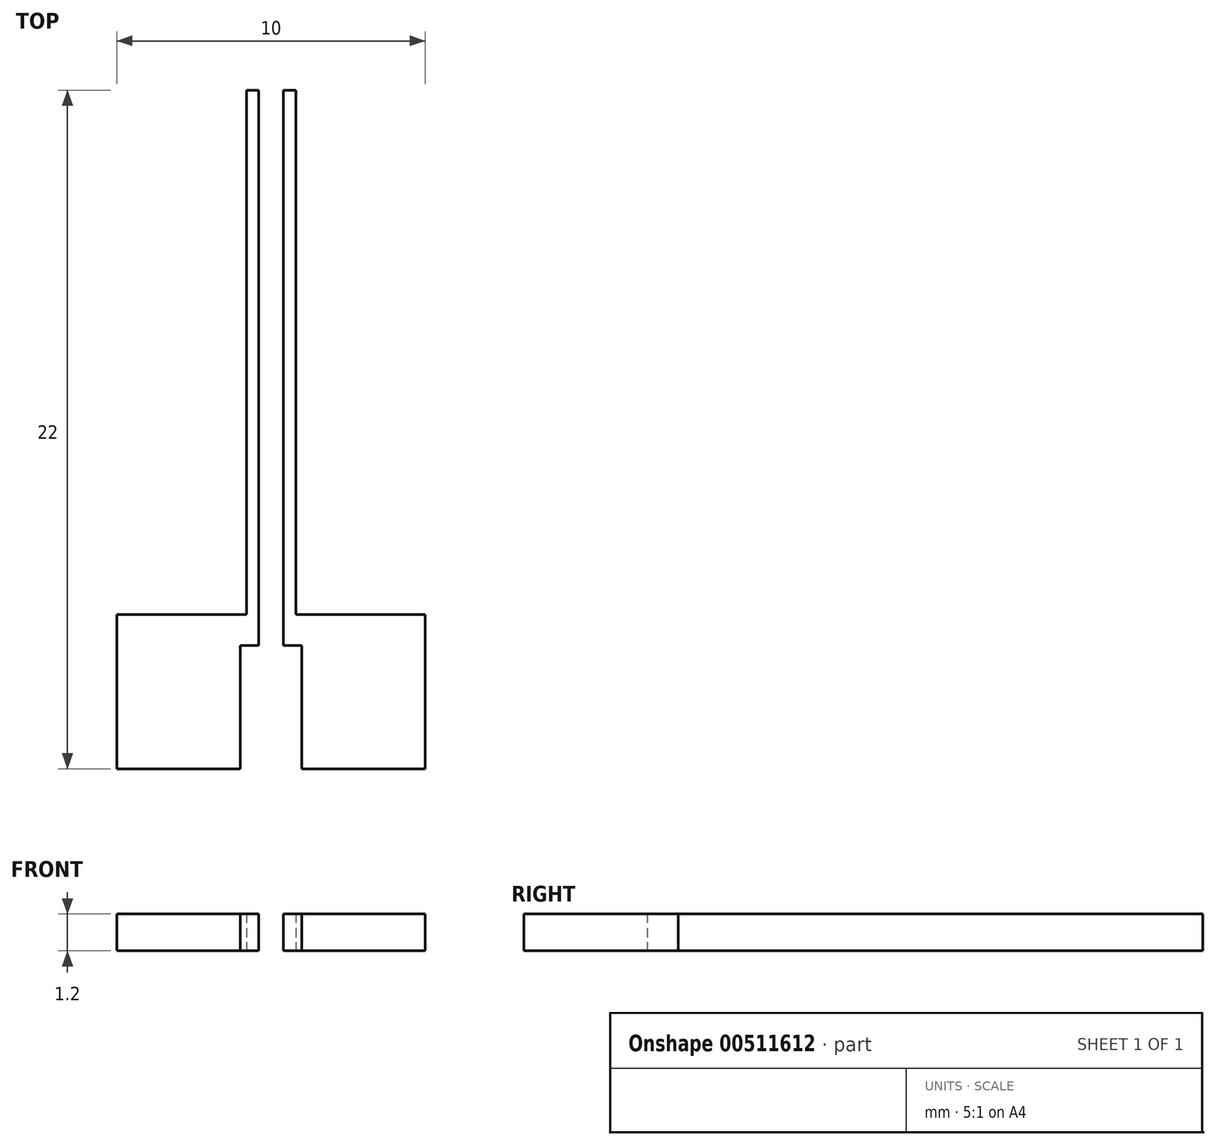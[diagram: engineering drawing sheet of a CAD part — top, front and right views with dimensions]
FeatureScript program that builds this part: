
annotation { "Feature Type Name" : "Feature", "Feature Type Description" : "" }
export const myFeature = defineFeature(function(context is Context, id is Id, definition is map)
    precondition{}
    {
        {
            var Q0;
            Q0=qCreatedBy(makeId("Top.planeOp"),FACE);
            var sketch = newSketch(context, id + "F0", { "sketchPlane" : qUnion([Q0])});
            skLineSegment(sketch, "E0", {"start": v(0, 0) * mm, "end": v(0.6, 0) * mm});
            skLineSegment(sketch, "E1.bottom", {"start": v(0.8, 11) * mm, "end": v(0.4, 11) * mm});
            skLineSegment(sketch, "E1.top", {"start": v(0.8, -11) * mm, "end": v(0.4, -11) * mm});
            skLineSegment(sketch, "E1.left", {"start": v(0.8, 11) * mm, "end": v(0.8, -11) * mm});
            skLineSegment(sketch, "E1.right", {"start": v(0.4, 11) * mm, "end": v(0.4, -11) * mm});
            skPoint(sketch, "E1.middle", {"position": v(0.6, 0) * mm});
            skLineSegment(sketch, "E2", {"start": v(0, -11) * mm, "end": v(0, -6) * mm});
            skLineSegment(sketch, "E3", {"start": v(0, -6) * mm, "end": v(1, -6) * mm});
            skLineSegment(sketch, "E4", {"start": v(1, -6) * mm, "end": v(5, -6) * mm});
            skLineSegment(sketch, "E5", {"start": v(5, -6) * mm, "end": v(5, -11) * mm});
            skLineSegment(sketch, "E6", {"start": v(5, -11) * mm, "end": v(0, -11) * mm});
            skLineSegment(sketch, "E7", {"start": v(0, -6) * mm, "end": v(0.5, -6) * mm});
            skLineSegment(sketch, "E8", {"start": v(1, -6) * mm, "end": v(1, -7) * mm});
            skLineSegment(sketch, "E9", {"start": v(1, -7) * mm, "end": v(0.4, -7) * mm});
            skLineSegment(sketch, "E10", {"start": v(1, -7) * mm, "end": v(1, -11) * mm});
            skLineSegment(sketch, "E11.MirrorCS", {"start": v(-0.4, 11) * mm, "end": v(-0.4, -11) * mm});
            skLineSegment(sketch, "E12.MirrorCS", {"start": v(-0.8, 11) * mm, "end": v(-0.8, -11) * mm});
            skLineSegment(sketch, "E13.MirrorCS", {"start": v(-1, -6) * mm, "end": v(-5, -6) * mm});
            skLineSegment(sketch, "E14.MirrorCS", {"start": v(-5, -6) * mm, "end": v(-5, -11) * mm});
            skLineSegment(sketch, "E15.MirrorCS", {"start": v(-5, -11) * mm, "end": v(0, -11) * mm});
            skLineSegment(sketch, "E16.MirrorCS", {"start": v(0, -6) * mm, "end": v(-1, -6) * mm});
            skLineSegment(sketch, "E17.MirrorCS", {"start": v(-0.8, 11) * mm, "end": v(-0.4, 11) * mm});
            skLineSegment(sketch, "E18.MirrorCS", {"start": v(-1, -7) * mm, "end": v(-0.4, -7) * mm});
            skLineSegment(sketch, "E19.MirrorCS", {"start": v(-1, -6) * mm, "end": v(-1, -7) * mm});
            skLineSegment(sketch, "E20.MirrorCS", {"start": v(-1, -7) * mm, "end": v(-1, -11) * mm});
            skSolve(sketch);
        }
        {
            var Q0;
            {var subQ6=sQuery(id+"F0.wireOp",EDGE,"E1.bottom");Q0=makeQuery(id+"F0.imprint","IMPRINT",FACE,{"disambiguationData":[TD([[makeQuery(id+"F0.imprint","IMPRINT",EDGE,{"derivedFrom":subQ6}),1.0]])]});}
            var Q1;
            {var subQ0=sQuery(id+"F0.wireOp",EDGE,"E17.MirrorCS");Q1=makeQuery(id+"F0.imprint","IMPRINT",FACE,{"disambiguationData":[TD([[makeQuery(id+"F0.imprint","IMPRINT",EDGE,{"derivedFrom":subQ0}),-1.0]])]});}
            var Q2;
            Q2=makeQuery(id+"F0.imprint","IMPRINT",FACE,{"disambiguationData":[TD([[makeQuery(id+"F0.imprint","IMPRINT",EDGE,{"derivedFrom":sQuery(id+"F0.wireOp",EDGE,"E4")}),-1.0]])]});
            var Q3;
            Q3=makeQuery(id+"F0.imprint","IMPRINT",FACE,{"disambiguationData":[TD([[makeQuery(id+"F0.imprint","IMPRINT",EDGE,{"derivedFrom":sQuery(id+"F0.wireOp",EDGE,"E13.MirrorCS")}),1.0]])]});
            var Q4;
            {var subQ5=sQuery(id+"F0.wireOp",EDGE,"E8");Q4=makeQuery(id+"F0.imprint","IMPRINT",FACE,{"disambiguationData":[TD([[makeQuery(id+"F0.imprint","IMPRINT",EDGE,{"derivedFrom":subQ5}),-1.0]])]});}
            var Q5;
            {var subQ5=sQuery(id+"F0.wireOp",EDGE,"E19.MirrorCS");Q5=makeQuery(id+"F0.imprint","IMPRINT",FACE,{"disambiguationData":[TD([[makeQuery(id+"F0.imprint","IMPRINT",EDGE,{"derivedFrom":subQ5}),1.0]])]});}
            var Q6;
            {var subQ1=sQuery(id+"F0.wireOp",EDGE,"E3");var subQ3=sQuery(id+"F0.wireOp",EDGE,"E1.left");var subQ4=makeQuery(id+"F0.imprint","INTERSECT",VERTEX,{"derivedFrom":[subQ3,subQ1]});Q6=makeQuery(id+"F0.imprint","IMPRINT",FACE,{"disambiguationData":[TD([[makeQuery(id+"F0.imprint","IMPRINT",EDGE,{"disambiguationData":[TD([[subQ4,-1.0]])],"derivedFrom":subQ3}),-1.0]])]});}
            var Q7;
            {var subQ0=sQuery(id+"F0.wireOp",EDGE,"E18.MirrorCS");var subQ1=sQuery(id+"F0.wireOp",EDGE,"E11.MirrorCS");var subQ2=makeQuery(id+"F0.imprint","INTERSECT",VERTEX,{"derivedFrom":[subQ1,subQ0]});Q7=makeQuery(id+"F0.imprint","IMPRINT",FACE,{"disambiguationData":[TD([[makeQuery(id+"F0.imprint","IMPRINT",EDGE,{"disambiguationData":[TD([[subQ2,1.0]])],"derivedFrom":subQ1}),-1.0]])]});}
            extrude(context, id + "F1", {"entities" : qUnion([Q0, Q1, Q2, Q3, Q4, Q5, Q6, Q7]), "depth" : 1.2 * mm, "offsetDistance" : 25 * mm});
        }
    });
